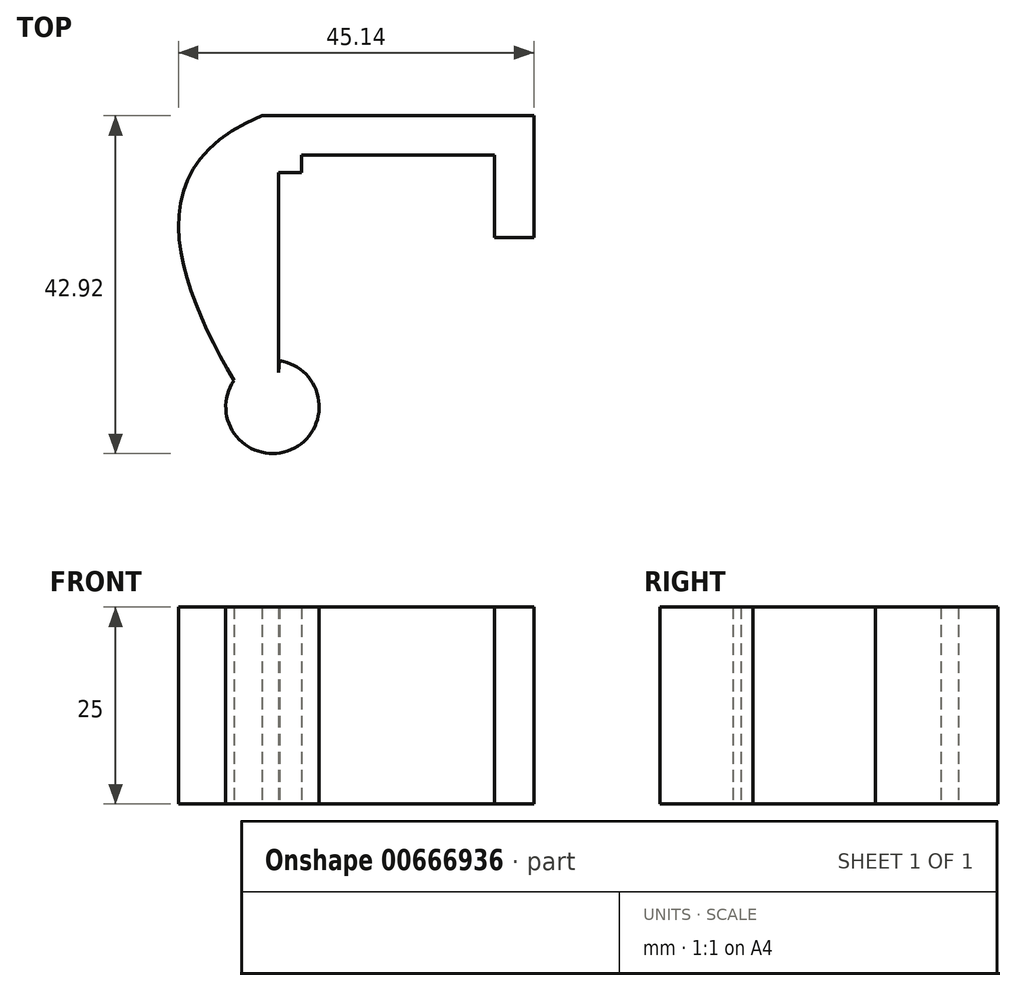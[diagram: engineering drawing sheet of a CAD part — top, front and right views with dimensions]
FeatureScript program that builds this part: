
annotation { "Feature Type Name" : "Feature", "Feature Type Description" : "" }
export const myFeature = defineFeature(function(context is Context, id is Id, definition is map)
    precondition{}
    {
        {
            var Q0;
            Q0=qCreatedBy(makeId("Top.planeOp"),FACE);
            var sketch = newSketch(context, id + "F0", { "sketchPlane" : qUnion([Q0])});
            skLineSegment(sketch, "E0.bottom", {"start": v(12.25, -5.25) * mm, "end": v(-12.25, -5.25) * mm});
            skLineSegment(sketch, "E0.top", {"start": v(12.25, 5.25) * mm, "end": v(-12.25, 5.25) * mm});
            skLineSegment(sketch, "E0.left", {"start": v(12.25, -5.25) * mm, "end": v(12.25, 5.25) * mm});
            skLineSegment(sketch, "E0.right", {"start": v(-12.25, -5.25) * mm, "end": v(-12.25, 5.25) * mm});
            skPoint(sketch, "E0.middle", {"position": v(0, 0) * mm});
            skLineSegment(sketch, "E1.1", {"start": v(17.25, 10.25) * mm, "end": v(-17.29, 10.25) * mm});
            skLineSegment(sketch, "E1.2", {"start": v(17.25, -5.25) * mm, "end": v(17.25, 10.25) * mm});
            skLineSegment(sketch, "E2", {"start": v(12.25, -5.25) * mm, "end": v(17.25, -5.25) * mm});
            skLineSegment(sketch, "E3", {"start": v(-12.25, -5.25) * mm, "end": v(-12.25, -29.4) * mm});
            skFitSpline(sketch, "E4", {"points": [v(-17.29, 10.25) * mm, v(-17.29, -29.4) * mm], "startDerivative": vector(-58.91, -24.04) * mm, "endDerivative": vector(22.06, -36.38) * mm});
            skFitSpline(sketch, "E5.0", {"points": [v(-15.25, 5.25) * mm, v(-16.25, 4.84) * mm, v(-17.98, 3.98) * mm, v(-19.8, 2.66) * mm, v(-21, 1.36) * mm, v(-21.78, 0.08) * mm, v(-22.27, -1.3) * mm, v(-22.51, -2.91) * mm, v(-22.49, -4.79) * mm, v(-22.17, -6.9) * mm, v(-21.57, -9.21) * mm, v(-20.42, -12.47) * mm, v(-18.43, -16.76) * mm, v(-15.56, -21.87) * mm, v(-13.6, -25.08) * mm, v(-12.67, -26.6) * mm]});
            skLineSegment(sketch, "E6", {"start": v(-15.21, -22.38) * mm, "end": v(-12.25, 5.25) * mm});
            skCircle(sketch, "E7", {"center": v(-15.95, -26.74) * mm, "radius": 5.93 * mm});
            skLineSegment(sketch, "E8", {"start": v(-12.25, 3.03) * mm, "end": v(-15.21, 3.03) * mm});
            skLineSegment(sketch, "E9", {"start": v(-15.21, 3.03) * mm, "end": v(-15.21, -22.38) * mm});
            skLineSegment(sketch, "E10", {"start": v(-17.29, 10.25) * mm, "end": v(0, 104.89) * mm});
            skSolve(sketch);
        }
        {
            var Q0;
            {var subQ0=sQuery(id+"F0.wireOp",EDGE,"QykBEQsn-hCWK-UVyP-jZXi-G9f6QpuQl3UA");Q0=makeQuery(id+"F0.imprint","IMPRINT",FACE,{"disambiguationData":[TD([[makeQuery(id+"F0.imprint","IMPRINT",EDGE,{"derivedFrom":subQ0}),-1.0]])]});}
            var Q1;
            Q1=makeQuery(id+"F0.imprint","IMPRINT",FACE,{"disambiguationData":[TD([[makeQuery(id+"F0.imprint","IMPRINT",EDGE,{"derivedFrom":sQuery(id+"F0.wireOp",EDGE,"E0.top")}),-1.0]])]});
            var Q2;
            {var subQ0=sQuery(id+"F0.wireOp",EDGE,"E7");var subQ1=makeQuery(id+"F0.imprint","INTERSECT",VERTEX,{"derivedFrom":[sQuery(id+"F0.wireOp",EDGE,"E3"),subQ0]});Q2=makeQuery(id+"F0.imprint","IMPRINT",FACE,{"disambiguationData":[TD([[makeQuery(id+"F0.imprint","IMPRINT",EDGE,{"disambiguationData":[TD([[subQ1,-1.0]])],"derivedFrom":subQ0}),1.0]])]});}
            var Q3;
            {var subQ0=sQuery(id+"F0.wireOp",EDGE,"E6");Q3=makeQuery(id+"F0.imprint","IMPRINT",FACE,{"disambiguationData":[TD([[makeQuery(id+"F0.imprint","IMPRINT",EDGE,{"derivedFrom":subQ0}),-1.0]])]});}
            extrude(context, id + "F1", {"entities" : qUnion([Q0, Q1, Q2, Q3]), "depth" : 25 * mm, "offsetDistance" : 25 * mm});
        }
    });
